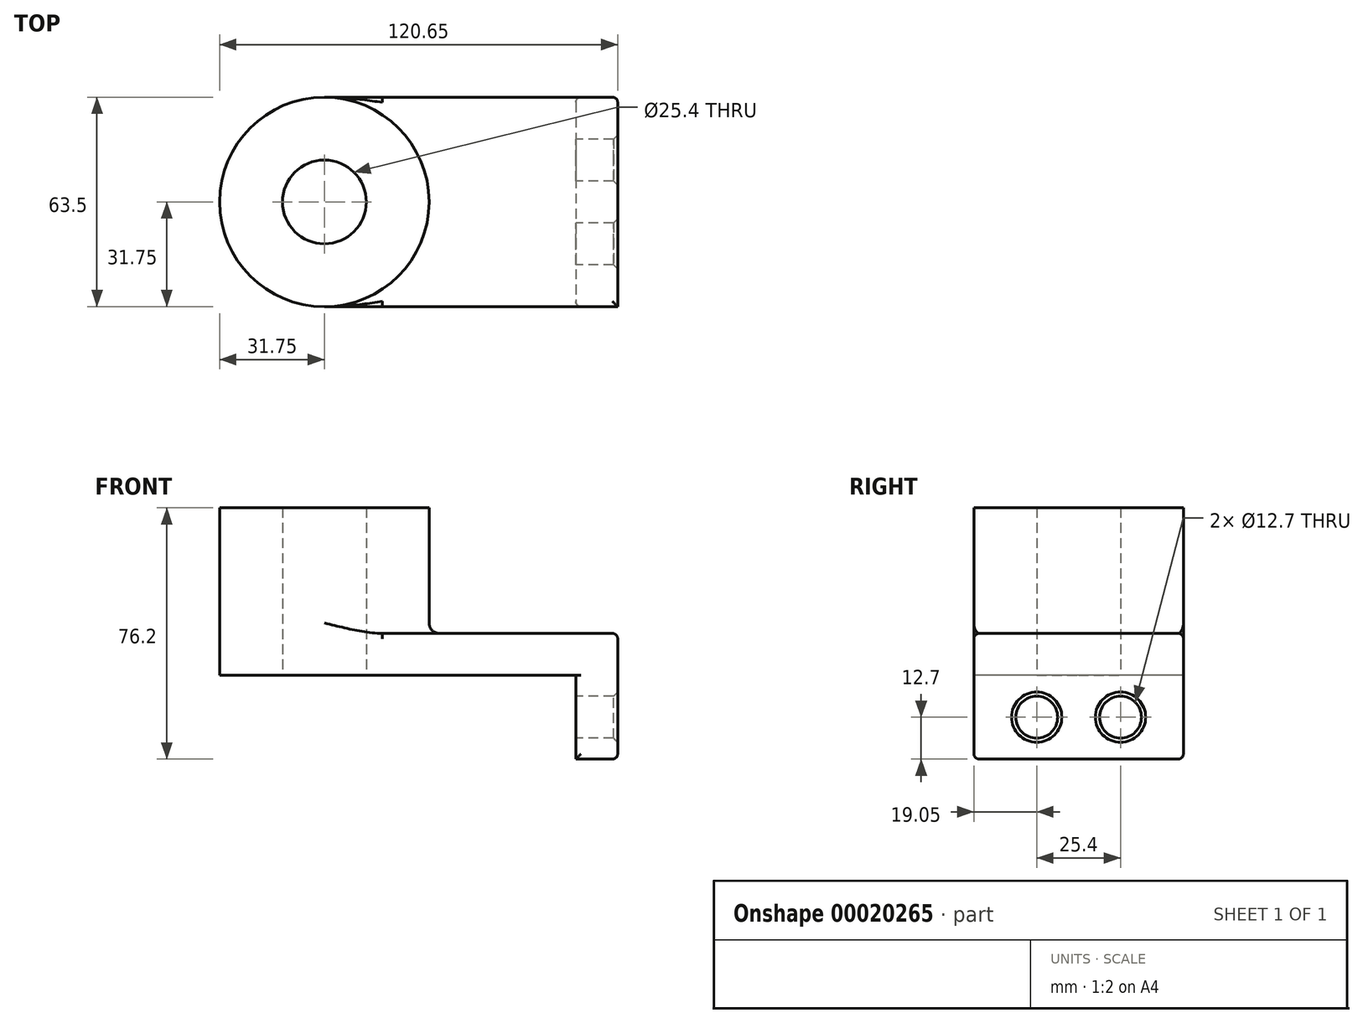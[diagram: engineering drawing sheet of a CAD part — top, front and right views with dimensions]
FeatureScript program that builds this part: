
annotation { "Feature Type Name" : "Feature", "Feature Type Description" : "" }
export const myFeature = defineFeature(function(context is Context, id is Id, definition is map)
    precondition{}
    {
        {
            var Q0;
            Q0=qCreatedBy(makeId("Top.planeOp"),FACE);
            var sketch = newSketch(context, id + "F0", { "sketchPlane" : qUnion([Q0])});
            skLineSegment(sketch, "E0.rect.bottom", {"start": v(-38.1, 31.75) * mm, "end": v(38.1, 31.75) * mm});
            skLineSegment(sketch, "E0.rect.top", {"start": v(-38.1, -31.75) * mm, "end": v(38.1, -31.75) * mm});
            skLineSegment(sketch, "E0.rect.left", {"start": v(-38.1, 31.75) * mm, "end": v(-38.1, -31.75) * mm});
            skLineSegment(sketch, "E0.rect.right", {"start": v(38.1, 31.75) * mm, "end": v(38.1, -31.75) * mm});
            skPoint(sketch, "E0.rect.middle", {"position": v(0, 0) * mm});
            skCircle(sketch, "E1", {"center": v(-38.1, 0) * mm, "radius": 31.75 * mm});
            skCircle(sketch, "E2", {"center": v(-38.1, 0) * mm, "radius": 12.7 * mm});
            skSolve(sketch);
        }
        {
            var Q0;
            Q0 = qSketchRegion(id + "F0", true);
            extrude(context, id + "F1", {"entities" : qUnion([Q0]), "depth" : 12.7 * mm});
        }
        {
            var Q0;
            Q0=makeQuery(id+"F1.opExtrude","SWEPT_FACE",FACE,{"disambiguationData":[OSD([sQuery(id+"F0.wireOp",EDGE,"E0.rect.right")])]});
            var sketch = newSketch(context, id + "F2", { "sketchPlane" : qUnion([Q0])});
            skLineSegment(sketch, "E3.bottom", {"start": v(-31.75, 12.7) * mm, "end": v(31.75, 12.7) * mm});
            skLineSegment(sketch, "E3.top", {"start": v(-31.75, -25.4) * mm, "end": v(31.75, -25.4) * mm});
            skLineSegment(sketch, "E3.left", {"start": v(-31.75, 12.7) * mm, "end": v(-31.75, -25.4) * mm});
            skLineSegment(sketch, "E3.right", {"start": v(31.75, 12.7) * mm, "end": v(31.75, -25.4) * mm});
            skCircle(sketch, "E4", {"center": v(-12.7, -12.7) * mm, "radius": 6.35 * mm});
            skLineSegment(sketch, "E5", {"start": v(0, 0) * mm, "end": v(0, -25.4) * mm, "construction": true});
            skCircle(sketch, "E6.MirrorC", {"center": v(12.7, -12.7) * mm, "radius": 6.35 * mm});
            skSolve(sketch);
        }
        {
            var Q0;
            Q0 = qSketchRegion(id + "F2", true);
            extrude(context, id + "F3", {"entities" : qUnion([Q0]), "operationType" : NewBodyOperationType.ADD, "depth" : 12.7 * mm});
        }
        {
            var Q0;
            {var subQ0=sQuery(id+"F0.wireOp",EDGE,"E2");var subQ1=sQuery(id+"F0.wireOp",EDGE,"E0.rect.left");var subQ3=makeQuery(id+"F0.imprint","INTERSECT",VERTEX,{"disambiguationData":[OD(0.0)],"derivedFrom":[subQ1,subQ0]});Q0=makeQuery(id+"F0.imprint","IMPRINT",FACE,{"disambiguationData":[TD([[makeQuery(id+"F0.imprint","IMPRINT",EDGE,{"disambiguationData":[TD([[subQ3,-1.0]])],"derivedFrom":subQ0}),-1.0]])]});}
            var Q1;
            {var subQ0=sQuery(id+"F0.wireOp",EDGE,"E2");var subQ1=sQuery(id+"F0.wireOp",EDGE,"E0.rect.left");var subQ3=makeQuery(id+"F0.imprint","INTERSECT",VERTEX,{"disambiguationData":[OD(0.0)],"derivedFrom":[subQ1,subQ0]});Q1=makeQuery(id+"F0.imprint","IMPRINT",FACE,{"disambiguationData":[TD([[makeQuery(id+"F0.imprint","IMPRINT",EDGE,{"disambiguationData":[TD([[subQ3,1.0]])],"derivedFrom":subQ0}),-1.0]])]});}
            extrude(context, id + "F4", {"entities" : qUnion([Q0, Q1]), "operationType" : NewBodyOperationType.ADD, "depth" : 50.8 * mm});
        }
        {
            var Q0;
            {var subQ0=sQuery(id+"F0.wireOp",EDGE,"E1");Q0=makeQuery(id+"F4.boolean.opBoolean","INTERSECT",EDGE,{"derivedFrom":[makeQuery(id+"F3.boolean.opBoolean","MERGE",FACE,{"derivedFrom":[makeQuery(id+"F1.opExtrude","CAP_FACE",FACE,{"disambiguationData":[OSD([sQuery(id+"F0.wireOp",EDGE,"E0.rect.bottom"),sQuery(id+"F0.wireOp",EDGE,"E0.rect.top"),sQuery(id+"F0.wireOp",EDGE,"E0.rect.right"),subQ0,sQuery(id+"F0.wireOp",EDGE,"E2")])],"isStart":false}),makeQuery(id+"F3.opExtrude","SWEPT_FACE",FACE,{"disambiguationData":[OSD([sQuery(id+"F2.wireOp",EDGE,"E3.bottom")])]})]}),makeQuery(id+"F4.opExtrude","SWEPT_FACE",FACE,{"disambiguationData":[OSD([subQ0])]})]});}
            fillet(context, id + "F5", {"entities" : qUnion([Q0]), "radius" : 3.17 * mm, "tangentPropagation" : true, "allowEdgeOverflow" : false});
        }
        {
            var Q0;
            Q0=makeQuery(id+"F3.boolean.opBoolean","MERGE",EDGE,{"derivedFrom":[makeQuery(id+"F1.opExtrude","CAP_EDGE",EDGE,{"disambiguationData":[OSD([sQuery(id+"F0.wireOp",EDGE,"E0.rect.top")])],"isStart":false}),makeQuery(id+"F3.opExtrude","SWEPT_EDGE",EDGE,{"disambiguationData":[OSD([sQuery(id+"F2.wireOp",EDGE,"E3.bottom"),sQuery(id+"F2.wireOp",EDGE,"E3.left")])]})]});
            var Q1;
            Q1=makeQuery(id+"F3.opExtrude","CAP_EDGE",EDGE,{"disambiguationData":[OSD([sQuery(id+"F2.wireOp",EDGE,"E3.bottom")])],"isStart":false});
            var Q2;
            Q2=makeQuery(id+"F3.boolean.opBoolean","MERGE",EDGE,{"derivedFrom":[makeQuery(id+"F1.opExtrude","CAP_EDGE",EDGE,{"disambiguationData":[OSD([sQuery(id+"F0.wireOp",EDGE,"E0.rect.bottom")])],"isStart":false}),makeQuery(id+"F3.opExtrude","SWEPT_EDGE",EDGE,{"disambiguationData":[OSD([sQuery(id+"F2.wireOp",EDGE,"E3.bottom"),sQuery(id+"F2.wireOp",EDGE,"E3.right")])]})]});
            var Q3;
            Q3=makeQuery(id+"F3.opExtrude","CAP_EDGE",EDGE,{"disambiguationData":[OSD([sQuery(id+"F2.wireOp",EDGE,"E3.right")])],"isStart":false});
            var Q4;
            Q4=makeQuery(id+"F3.opExtrude","CAP_EDGE",EDGE,{"disambiguationData":[OSD([sQuery(id+"F2.wireOp",EDGE,"E3.top")])],"isStart":false});
            var Q5;
            Q5=makeQuery(id+"F3.opExtrude","SWEPT_EDGE",EDGE,{"disambiguationData":[OSD([sQuery(id+"F2.wireOp",EDGE,"E3.top"),sQuery(id+"F2.wireOp",EDGE,"E3.right")])]});
            var Q6;
            Q6=makeQuery(id+"F3.opExtrude","CAP_EDGE",EDGE,{"disambiguationData":[OSD([sQuery(id+"F2.wireOp",EDGE,"E3.right")])],"isStart":true});
            var Q7;
            Q7=makeQuery(id+"F3.opExtrude","CAP_EDGE",EDGE,{"disambiguationData":[OSD([sQuery(id+"F2.wireOp",EDGE,"E3.left")])],"isStart":true});
            var Q8;
            Q8=makeQuery(id+"F3.opExtrude","SWEPT_EDGE",EDGE,{"disambiguationData":[OSD([sQuery(id+"F2.wireOp",EDGE,"E3.top"),sQuery(id+"F2.wireOp",EDGE,"E3.left")])]});
            fillet(context, id + "F6", {"entities" : qUnion([Q0, Q1, Q2, Q3, Q4, Q5, Q6, Q7, Q8]), "radius" : 1.59 * mm, "tangentPropagation" : true, "allowEdgeOverflow" : false});
        }
        {
            var Q0;
            Q0=makeQuery(id+"FXfHJEmNmukatdD_1.opExtrude","CAP_FACE",FACE,{"disambiguationData":[OSD([sQuery(id+"F0.wireOp",EDGE,"E1"),sQuery(id+"F0.wireOp",EDGE,"E2")])],"isStart":false});
            var Q1;
            Q1=makeQuery(id+"F3.opExtrude","CAP_EDGE",EDGE,{"disambiguationData":[OSD([sQuery(id+"F2.wireOp",EDGE,"E4")])],"isStart":false});
            var Q2;
            Q2=makeQuery(id+"F3.opExtrude","CAP_EDGE",EDGE,{"disambiguationData":[OSD([sQuery(id+"F2.wireOp",EDGE,"E6.MirrorC")])],"isStart":false});
            chamfer(context, id + "F7", {"entities" : qUnion([Q0, Q1, Q2]), "width" : 1.27 * mm, "tangentPropagation" : true});
        }
    });
